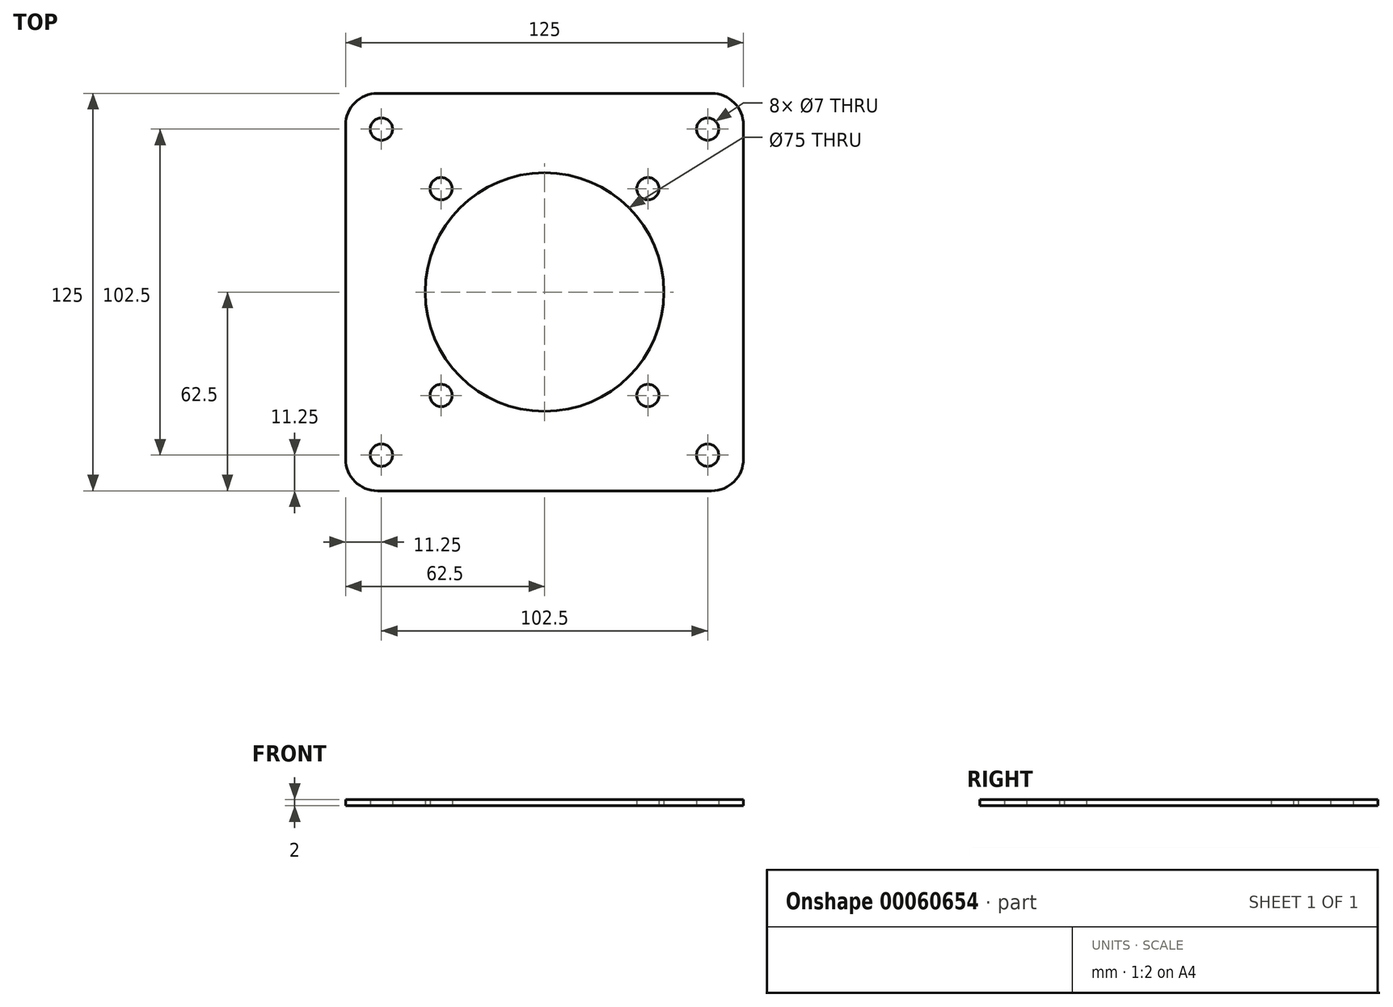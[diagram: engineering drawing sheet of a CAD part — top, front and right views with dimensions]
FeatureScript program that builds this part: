
annotation { "Feature Type Name" : "Feature", "Feature Type Description" : "" }
export const myFeature = defineFeature(function(context is Context, id is Id, definition is map)
    precondition{}
    {
        {
            var Q0;
            Q0=qCreatedBy(makeId("Top.planeOp"),FACE);
            var sketch = newSketch(context, id + "F0", { "sketchPlane" : qUnion([Q0])});
            skLineSegment(sketch, "E0.rect.bottom", {"start": v(62.5, 62.5) * mm, "end": v(-62.5, 62.5) * mm});
            skLineSegment(sketch, "E0.rect.top", {"start": v(62.5, -62.5) * mm, "end": v(-62.5, -62.5) * mm});
            skLineSegment(sketch, "E0.rect.left", {"start": v(62.5, 62.5) * mm, "end": v(62.5, -62.5) * mm});
            skLineSegment(sketch, "E0.rect.right", {"start": v(-62.5, 62.5) * mm, "end": v(-62.5, -62.5) * mm});
            skPoint(sketch, "E0.rect.middle", {"position": v(0, 0) * mm});
            skCircle(sketch, "E1", {"center": v(0, 0) * mm, "radius": 37.5 * mm});
            skSolve(sketch);
        }
        {
            var Q0;
            Q0 = qSketchRegion(id + "F0", true);
            extrude(context, id + "F1", {"entities" : qUnion([Q0]), "depth" : 2 * mm});
        }
        {
            var Q0;
            Q0=qCreatedBy(makeId("Top.planeOp"),FACE);
            var sketch = newSketch(context, id + "F2", { "sketchPlane" : qUnion([Q0])});
            skLineSegment(sketch, "E2.rect.bottom", {"start": v(51.25, 51.25) * mm, "end": v(-51.25, 51.25) * mm, "construction": true});
            skLineSegment(sketch, "E2.rect.top", {"start": v(51.25, -51.25) * mm, "end": v(-51.25, -51.25) * mm, "construction": true});
            skLineSegment(sketch, "E2.rect.left", {"start": v(51.25, 51.25) * mm, "end": v(51.25, -51.25) * mm, "construction": true});
            skLineSegment(sketch, "E2.rect.right", {"start": v(-51.25, 51.25) * mm, "end": v(-51.25, -51.25) * mm, "construction": true});
            skPoint(sketch, "E2.rect.middle", {"position": v(0, 0) * mm});
            skCircle(sketch, "E3", {"center": v(-51.25, 51.25) * mm, "radius": 3.5 * mm});
            skCircle(sketch, "E4", {"center": v(51.25, 51.25) * mm, "radius": 3.5 * mm});
            skCircle(sketch, "E5", {"center": v(-51.25, -51.25) * mm, "radius": 3.5 * mm});
            skCircle(sketch, "E6", {"center": v(51.25, -51.25) * mm, "radius": 3.5 * mm});
            skLineSegment(sketch, "E7.rect.bottom", {"start": v(32.5, 32.5) * mm, "end": v(-32.5, 32.5) * mm, "construction": true});
            skLineSegment(sketch, "E7.rect.top", {"start": v(32.5, -32.5) * mm, "end": v(-32.5, -32.5) * mm, "construction": true});
            skLineSegment(sketch, "E7.rect.left", {"start": v(32.5, 32.5) * mm, "end": v(32.5, -32.5) * mm, "construction": true});
            skLineSegment(sketch, "E7.rect.right", {"start": v(-32.5, 32.5) * mm, "end": v(-32.5, -32.5) * mm, "construction": true});
            skCircle(sketch, "E8", {"center": v(-32.5, 32.5) * mm, "radius": 3.5 * mm});
            skCircle(sketch, "E9", {"center": v(32.5, 32.5) * mm, "radius": 3.5 * mm});
            skCircle(sketch, "E10", {"center": v(-32.5, -32.5) * mm, "radius": 3.5 * mm});
            skCircle(sketch, "E11", {"center": v(32.5, -32.5) * mm, "radius": 3.5 * mm});
            skSolve(sketch);
        }
        {
            var Q0;
            Q0 = qSketchRegion(id + "F2", true);
            extrude(context, id + "F3", {"entities" : qUnion([Q0]), "operationType" : NewBodyOperationType.REMOVE, "endBound" : BoundingType.THROUGH_ALL, "depth" : 25 * mm});
        }
        {
            var Q0;
            Q0=makeQuery(id+"F1.opExtrude","SWEPT_EDGE",EDGE,{"disambiguationData":[OSD([sQuery(id+"F0.wireOp",EDGE,"E0.rect.top"),sQuery(id+"F0.wireOp",EDGE,"E0.rect.left")])]});
            var Q1;
            Q1=makeQuery(id+"F1.opExtrude","SWEPT_EDGE",EDGE,{"disambiguationData":[OSD([sQuery(id+"F0.wireOp",EDGE,"E0.rect.bottom"),sQuery(id+"F0.wireOp",EDGE,"E0.rect.left")])]});
            var Q2;
            Q2=makeQuery(id+"F1.opExtrude","SWEPT_EDGE",EDGE,{"disambiguationData":[OSD([sQuery(id+"F0.wireOp",EDGE,"E0.rect.top"),sQuery(id+"F0.wireOp",EDGE,"E0.rect.right")])]});
            var Q3;
            Q3=makeQuery(id+"F1.opExtrude","SWEPT_EDGE",EDGE,{"disambiguationData":[OSD([sQuery(id+"F0.wireOp",EDGE,"E0.rect.bottom"),sQuery(id+"F0.wireOp",EDGE,"E0.rect.right")])]});
            fillet(context, id + "F4", {"entities" : qUnion([Q0, Q1, Q2, Q3]), "radius" : 10 * mm, "tangentPropagation" : true, "allowEdgeOverflow" : false});
        }
    });
